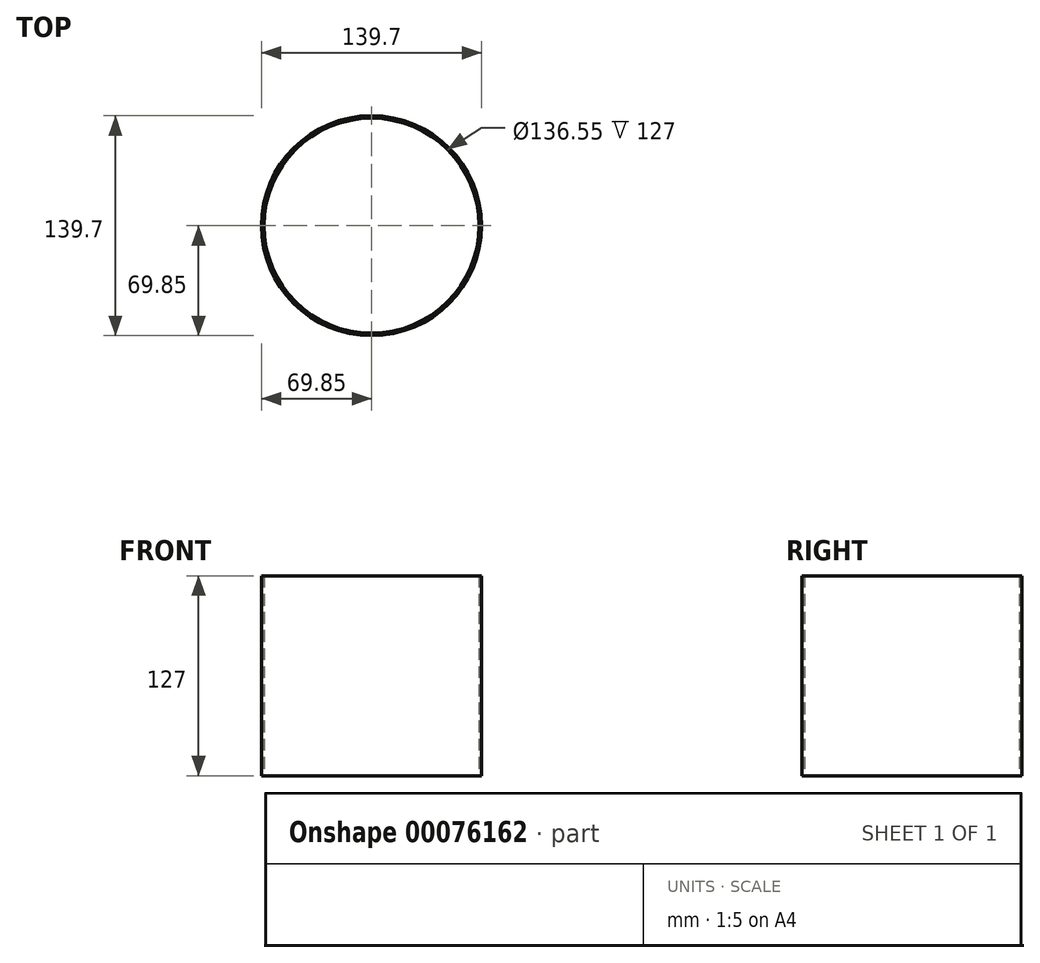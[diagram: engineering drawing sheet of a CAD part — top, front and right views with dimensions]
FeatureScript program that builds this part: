
annotation { "Feature Type Name" : "Feature", "Feature Type Description" : "" }
export const myFeature = defineFeature(function(context is Context, id is Id, definition is map)
    precondition{}
    {
        {
            var Q0;
            Q0=qCreatedBy(makeId("Top.planeOp"),FACE);
            var sketch = newSketch(context, id + "F0", { "sketchPlane" : qUnion([Q0])});
            skCircle(sketch, "E0", {"center": v(0, 0) * mm, "radius": 69.85 * mm});
            skSolve(sketch);
        }
        {
            var Q0;
            Q0 = qSketchRegion(id + "F0", true);
            extrude(context, id + "F1", {"entities" : qUnion([Q0]), "depth" : 127 * mm, "offsetDistance" : 25.4 * mm});
        }
        {
            var Q0;
            Q0=makeQuery(id+"F1.opExtrude","CAP_FACE",FACE,{"disambiguationData":[OSD([sQuery(id+"F0.wireOp",EDGE,"E0")])],"isStart":false});
            var Q1;
            Q1=makeQuery(id+"F1.opExtrude","CAP_FACE",FACE,{"disambiguationData":[OSD([sQuery(id+"F0.wireOp",EDGE,"E0")])],"isStart":true});
            shell(context, id + "F2", {"entities" : qUnion([Q0, Q1]), "thickness" : 1.57 * mm});
        }
    });
